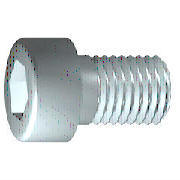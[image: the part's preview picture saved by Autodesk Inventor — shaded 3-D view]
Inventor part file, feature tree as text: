
AUTODESK INVENTOR PART (.ipt)
format: ipt  version: 2013 (Build 170138000, 138)  size: 177,152 bytes
history: native  units: mm (DEFAULTED — no unit token found)
features: sketch x2, extrude x1, plane x1, fillet x1
ambient origin geometry x7: Origin, YZ Plane, XY Plane, X Axis, Y Axis, Z Axis, Center Point
bodies: Solid1 (feature_tree), Body (feature_tree)
feature tree (5):
  extrude  "Slot"  Depth=0.306825mm
  plane  "Work Plane1"
  fillet  "Fillet2"  Radius=3.0mm
  sketch  "Sketch1"  dims[d1=18.0mm d2=0.306825mm d3=3.0mm]
  sketch  "Sketch2"  dims[d4=1.5mm d5=60.0deg d6=3.0mm d7=3.0mm d8=2.886751mm d9=5.5mm d10=90.0deg d11=10.0mm d12=0.0mm d13=18.0mm d14=0.0mm d15=0.306725mm d16=0.306725mm d17=0.3mm d19=0.0mm d26=60.0mm d27=45.0deg d28=0.0mm d29=0.0mm d30=0.1mm]
